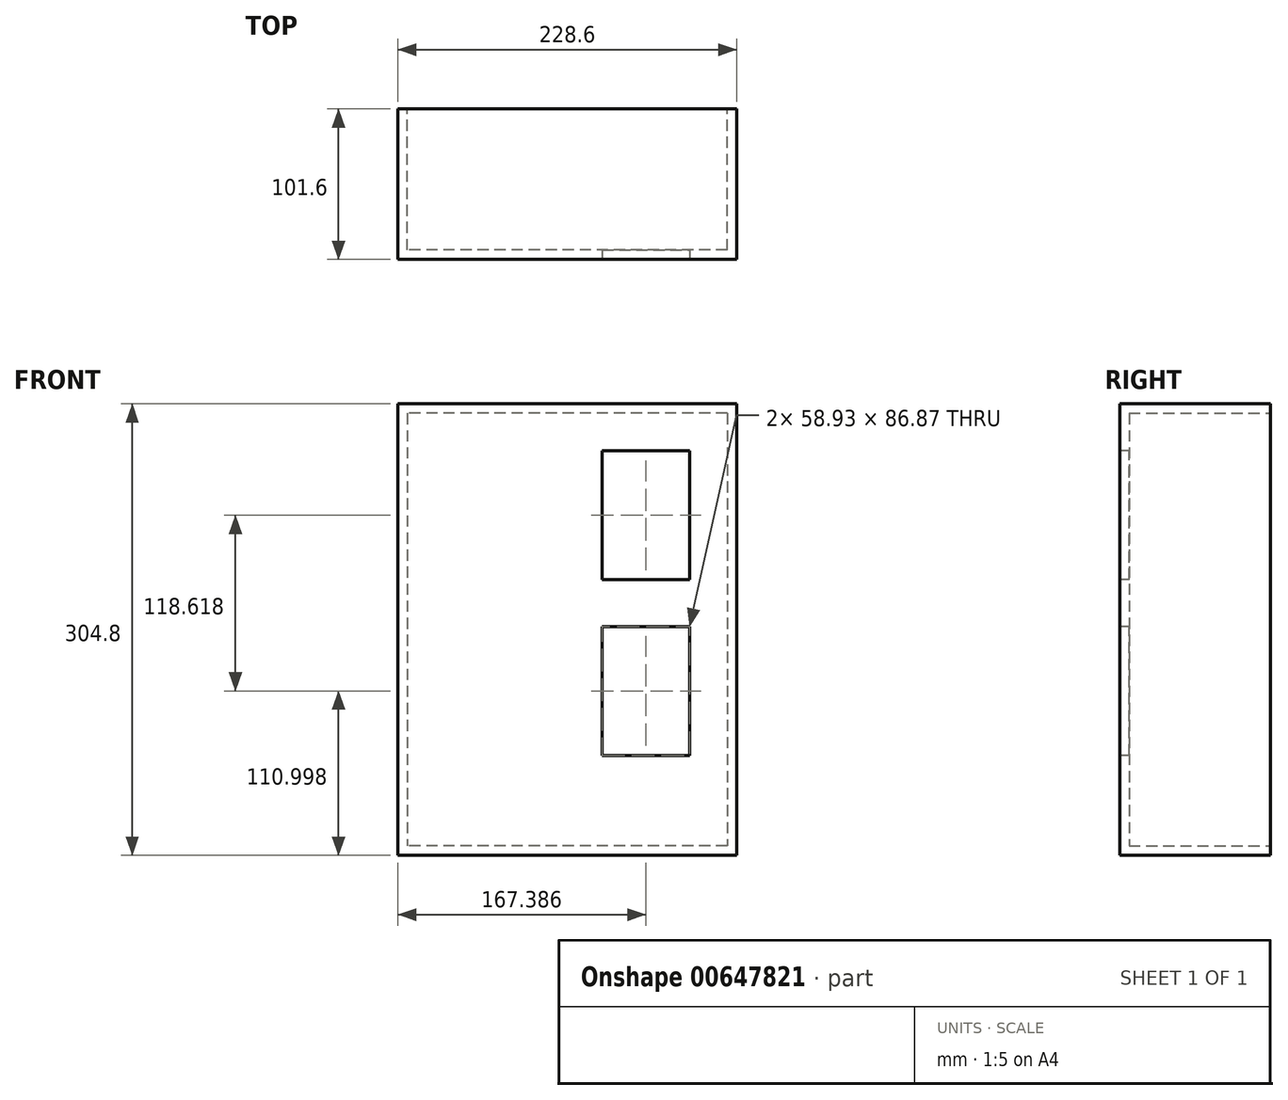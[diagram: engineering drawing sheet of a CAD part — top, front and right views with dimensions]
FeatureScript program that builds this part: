
annotation { "Feature Type Name" : "Feature", "Feature Type Description" : "" }
export const myFeature = defineFeature(function(context is Context, id is Id, definition is map)
    precondition{}
    {
        {
            var Q0;
            Q0=qCreatedBy(makeId("Top.planeOp"),FACE);
            var sketch = newSketch(context, id + "F0", { "sketchPlane" : qUnion([Q0])});
            skLineSegment(sketch, "E0.bottom", {"start": v(114.3, -50.8) * mm, "end": v(-114.3, -50.8) * mm});
            skLineSegment(sketch, "E0.top", {"start": v(114.3, 50.8) * mm, "end": v(-114.3, 50.8) * mm});
            skLineSegment(sketch, "E0.left", {"start": v(114.3, -50.8) * mm, "end": v(114.3, 50.8) * mm});
            skLineSegment(sketch, "E0.right", {"start": v(-114.3, -50.8) * mm, "end": v(-114.3, 50.8) * mm});
            skPoint(sketch, "E0.middle", {"position": v(0, 0) * mm});
            skSolve(sketch);
        }
        {
            var Q0;
            Q0=makeQuery(id+"F0.imprint","IMPRINT",FACE,{"disambiguationData":[TD([[makeQuery(id+"F0.imprint","IMPRINT",EDGE,{"derivedFrom":sQuery(id+"F0.wireOp",EDGE,"E0.bottom")}),-1.0]])]});
            extrude(context, id + "F1", {"entities" : qUnion([Q0]), "depth" : 304.8 * mm, "offsetDistance" : 25.4 * mm});
        }
        {
            var Q0;
            Q0=makeQuery(id+"F1.opExtrude","SWEPT_FACE",FACE,{"disambiguationData":[OSD([sQuery(id+"F0.wireOp",EDGE,"E0.top")])]});
            shell(context, id + "F2", {"entities" : qUnion([Q0]), "thickness" : 6.35 * mm});
        }
        {
            var Q0;
            Q0=makeQuery(id+"F1.opExtrude","SWEPT_FACE",FACE,{"disambiguationData":[OSD([sQuery(id+"F0.wireOp",EDGE,"E0.bottom")])]});
            var sketch = newSketch(context, id + "F3", { "sketchPlane" : qUnion([Q0])});
            skLineSegment(sketch, "E1.bottom", {"start": v(23.62, 186.18) * mm, "end": v(82.55, 186.18) * mm});
            skLineSegment(sketch, "E1.top", {"start": v(23.62, 273.05) * mm, "end": v(82.55, 273.05) * mm});
            skLineSegment(sketch, "E1.left", {"start": v(23.62, 186.18) * mm, "end": v(23.62, 273.05) * mm});
            skLineSegment(sketch, "E1.right", {"start": v(82.55, 186.18) * mm, "end": v(82.55, 273.05) * mm});
            skPoint(sketch, "E1.middle", {"position": v(53.09, 229.62) * mm});
            skLineSegment(sketch, "E2.bottom", {"start": v(23.62, 67.56) * mm, "end": v(82.55, 67.56) * mm});
            skLineSegment(sketch, "E2.top", {"start": v(23.62, 154.43) * mm, "end": v(82.55, 154.43) * mm});
            skLineSegment(sketch, "E2.left", {"start": v(23.62, 67.56) * mm, "end": v(23.62, 154.43) * mm});
            skLineSegment(sketch, "E2.right", {"start": v(82.55, 67.56) * mm, "end": v(82.55, 154.43) * mm});
            skPoint(sketch, "E2.middle", {"position": v(53.09, 111) * mm});
            skSolve(sketch);
        }
        {
            var Q0;
            Q0=makeQuery(id+"F3.imprint","IMPRINT",FACE,{"disambiguationData":[TD([[makeQuery(id+"F3.imprint","IMPRINT",EDGE,{"derivedFrom":sQuery(id+"F3.wireOp",EDGE,"E1.bottom")}),1.0]])]});
            var Q1;
            Q1=makeQuery(id+"F3.imprint","IMPRINT",FACE,{"disambiguationData":[TD([[makeQuery(id+"F3.imprint","IMPRINT",EDGE,{"derivedFrom":sQuery(id+"F3.wireOp",EDGE,"E2.bottom")}),1.0]])]});
            extrude(context, id + "F4", {"entities" : qUnion([Q0, Q1]), "operationType" : NewBodyOperationType.REMOVE, "oppositeDirection" : true, "depth" : 25.4 * mm, "offsetDistance" : 25.4 * mm});
        }
    });
